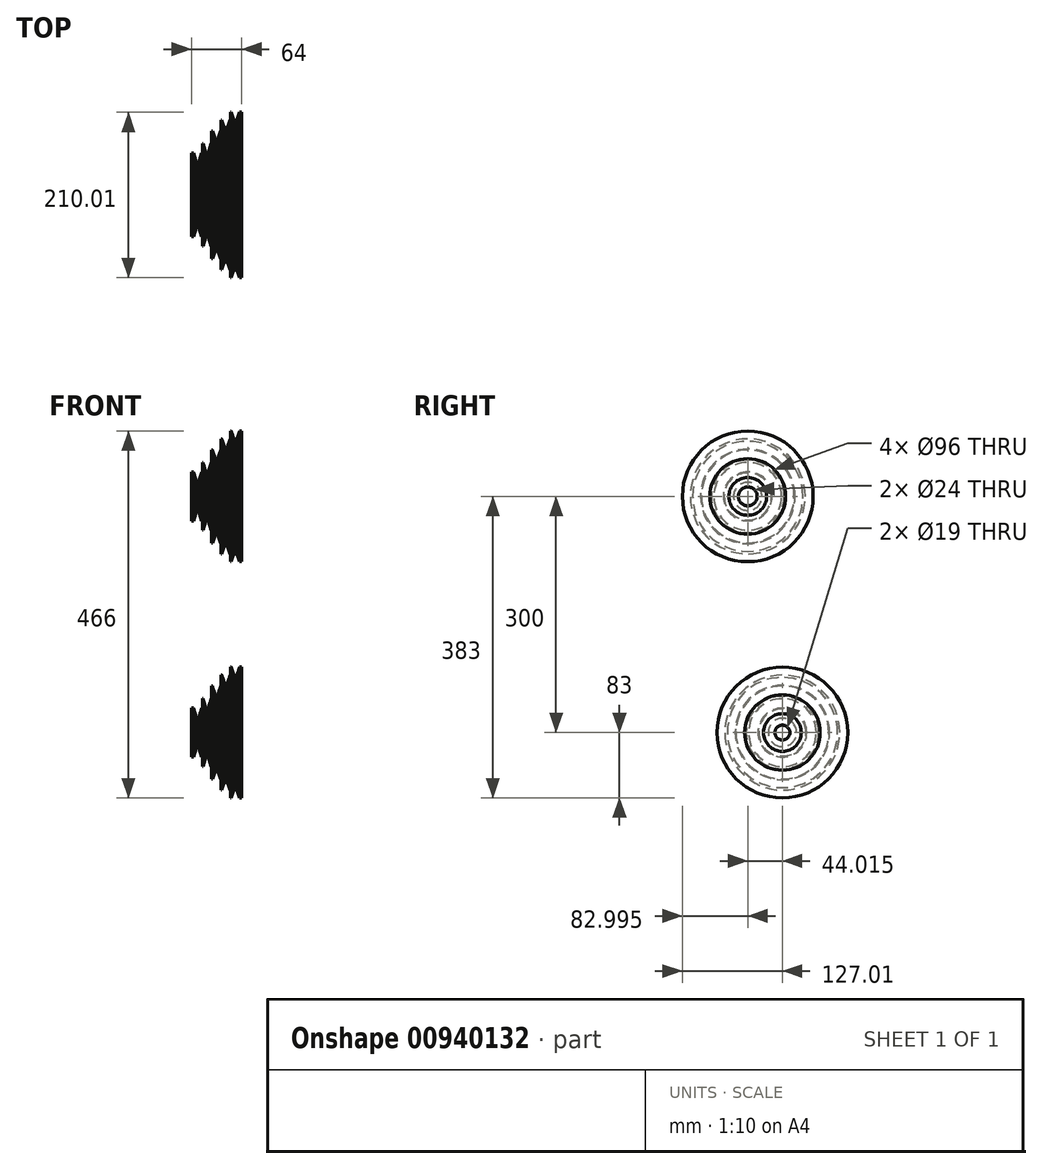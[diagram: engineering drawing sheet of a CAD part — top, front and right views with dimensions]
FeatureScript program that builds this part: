
annotation { "Feature Type Name" : "Feature", "Feature Type Description" : "" }
export const myFeature = defineFeature(function(context is Context, id is Id, definition is map)
    precondition{}
    {
        {
            var Q0;
            Q0=qCreatedBy(makeId("Top.planeOp"),FACE);
            var sketch = newSketch(context, id + "F0", { "sketchPlane" : qUnion([Q0])});
            skLineSegment(sketch, "E0", {"start": v(0, 0) * mm, "end": v(30, 0) * mm, "construction": true});
            skLineSegment(sketch, "E1", {"start": v(0, 0) * mm, "end": v(0, 31) * mm, "construction": true});
            skLineSegment(sketch, "E2", {"start": v(12, 0) * mm, "end": v(12, 31) * mm, "construction": true});
            skLineSegment(sketch, "E3", {"start": v(24, 0) * mm, "end": v(24, 43) * mm, "construction": true});
            skLineSegment(sketch, "E4", {"start": v(36, 0) * mm, "end": v(36, 59) * mm, "construction": true});
            skLineSegment(sketch, "E5", {"start": v(48, 0) * mm, "end": v(48, 73) * mm, "construction": true});
            skLineSegment(sketch, "E6", {"start": v(0, 31) * mm, "end": v(0.83, 31) * mm});
            skLineSegment(sketch, "E7", {"start": v(12, 43) * mm, "end": v(12.78, 43) * mm});
            skLineSegment(sketch, "E8", {"start": v(60, 0) * mm, "end": v(60, 83) * mm, "construction": true});
            skLineSegment(sketch, "E9", {"start": v(24, 59) * mm, "end": v(24.72, 59) * mm});
            skLineSegment(sketch, "E10", {"start": v(36, 73) * mm, "end": v(36.72, 73) * mm});
            skLineSegment(sketch, "E11", {"start": v(48, 83) * mm, "end": v(48.72, 83) * mm});
            skLineSegment(sketch, "E12", {"start": v(0, 28) * mm, "end": v(12, 28) * mm, "construction": true});
            skLineSegment(sketch, "E13", {"start": v(0, 18) * mm, "end": v(4.8, 18) * mm, "construction": true});
            skLineSegment(sketch, "E14", {"start": v(12, 40) * mm, "end": v(24, 40) * mm, "construction": true});
            skLineSegment(sketch, "E15", {"start": v(12, 30) * mm, "end": v(17, 30) * mm, "construction": true});
            skLineSegment(sketch, "E16", {"start": v(24, 56) * mm, "end": v(36, 56) * mm, "construction": true});
            skLineSegment(sketch, "E17", {"start": v(24, 46) * mm, "end": v(29.2, 46) * mm, "construction": true});
            skLineSegment(sketch, "E18", {"start": v(36, 70) * mm, "end": v(48, 70) * mm, "construction": true});
            skLineSegment(sketch, "E19", {"start": v(36, 60) * mm, "end": v(41.2, 60) * mm, "construction": true});
            skLineSegment(sketch, "E20", {"start": v(48, 80) * mm, "end": v(60, 80) * mm, "construction": true});
            skLineSegment(sketch, "E21", {"start": v(48, 70) * mm, "end": v(53.2, 70) * mm, "construction": true});
            skLineSegment(sketch, "E22", {"start": v(1.75, 28) * mm, "end": v(1.75, 28) * mm});
            skLineSegment(sketch, "E23", {"start": v(10.25, 28) * mm, "end": v(10.25, 28) * mm});
            skLineSegment(sketch, "E24", {"start": v(13.75, 40) * mm, "end": v(13.75, 30) * mm, "construction": true});
            skLineSegment(sketch, "E25", {"start": v(22.25, 40) * mm, "end": v(22.25, 30) * mm, "construction": true});
            skLineSegment(sketch, "E26", {"start": v(25.75, 56) * mm, "end": v(25.75, 46) * mm, "construction": true});
            skLineSegment(sketch, "E27", {"start": v(34.25, 56) * mm, "end": v(34.25, 46) * mm, "construction": true});
            skLineSegment(sketch, "E28", {"start": v(37.75, 70) * mm, "end": v(37.75, 60) * mm, "construction": true});
            skLineSegment(sketch, "E29", {"start": v(46.25, 70) * mm, "end": v(46.25, 60) * mm, "construction": true});
            skLineSegment(sketch, "E30", {"start": v(49.75, 80) * mm, "end": v(49.75, 70) * mm, "construction": true});
            skLineSegment(sketch, "E31", {"start": v(58.25, 80) * mm, "end": v(58.25, 70) * mm, "construction": true});
            skLineSegment(sketch, "E32", {"start": v(1.75, 28) * mm, "end": v(4.8, 18) * mm});
            skLineSegment(sketch, "E33", {"start": v(10.25, 28) * mm, "end": v(7.2, 18) * mm});
            skLineSegment(sketch, "E34", {"start": v(13.75, 40) * mm, "end": v(17, 30) * mm});
            skLineSegment(sketch, "E35", {"start": v(22.25, 40) * mm, "end": v(19, 30) * mm});
            skLineSegment(sketch, "E36", {"start": v(25.75, 56) * mm, "end": v(29.2, 46) * mm});
            skLineSegment(sketch, "E37", {"start": v(34.25, 56) * mm, "end": v(30.8, 46) * mm});
            skLineSegment(sketch, "E38", {"start": v(37.75, 70) * mm, "end": v(41.2, 60) * mm});
            skLineSegment(sketch, "E39", {"start": v(46.25, 70) * mm, "end": v(42.8, 60) * mm});
            skLineSegment(sketch, "E40", {"start": v(49.75, 80) * mm, "end": v(53.2, 70) * mm});
            skLineSegment(sketch, "E41", {"start": v(58.25, 80) * mm, "end": v(54.8, 70) * mm});
            skLineSegment(sketch, "E42", {"start": v(1.75, 28) * mm, "end": v(0.83, 31) * mm});
            skLineSegment(sketch, "E43", {"start": v(10.25, 28) * mm, "end": v(11.17, 31) * mm});
            skLineSegment(sketch, "E44", {"start": v(13.75, 40) * mm, "end": v(12.78, 43) * mm});
            skLineSegment(sketch, "E45", {"start": v(22.25, 40) * mm, "end": v(23.22, 43) * mm});
            skLineSegment(sketch, "E46", {"start": v(25.75, 56) * mm, "end": v(24.72, 59) * mm});
            skLineSegment(sketch, "E47", {"start": v(34.25, 56) * mm, "end": v(35.28, 59) * mm});
            skLineSegment(sketch, "E48", {"start": v(37.75, 70) * mm, "end": v(36.72, 73) * mm});
            skLineSegment(sketch, "E49", {"start": v(46.25, 70) * mm, "end": v(47.28, 73) * mm});
            skLineSegment(sketch, "E50", {"start": v(49.75, 80) * mm, "end": v(48.72, 83) * mm});
            skLineSegment(sketch, "E51", {"start": v(58.25, 80) * mm, "end": v(59.28, 83) * mm});
            skLineSegment(sketch, "E52", {"start": v(0.83, 31) * mm, "end": v(0.83, 31) * mm});
            skLineSegment(sketch, "E53", {"start": v(11.17, 31) * mm, "end": v(11.17, 31) * mm});
            skLineSegment(sketch, "E54", {"start": v(4.8, 18) * mm, "end": v(7.2, 18) * mm});
            skLineSegment(sketch, "E55", {"start": v(7.2, 18) * mm, "end": v(12, 18) * mm, "construction": true});
            skLineSegment(sketch, "E56", {"start": v(1.75, 28) * mm, "end": v(1.75, 18) * mm, "construction": true});
            skLineSegment(sketch, "E57", {"start": v(10.25, 28) * mm, "end": v(10.25, 18) * mm, "construction": true});
            skLineSegment(sketch, "E58", {"start": v(0.83, 31) * mm, "end": v(11.17, 31) * mm, "construction": true});
            skLineSegment(sketch, "E59", {"start": v(11.17, 31) * mm, "end": v(12, 31) * mm});
            skLineSegment(sketch, "E60", {"start": v(12.78, 43) * mm, "end": v(23.22, 43) * mm, "construction": true});
            skLineSegment(sketch, "E61", {"start": v(23.22, 43) * mm, "end": v(24, 43) * mm});
            skLineSegment(sketch, "E62", {"start": v(17, 30) * mm, "end": v(19, 30) * mm});
            skLineSegment(sketch, "E63", {"start": v(19, 30) * mm, "end": v(24, 30) * mm, "construction": true});
            skLineSegment(sketch, "E64", {"start": v(24.72, 59) * mm, "end": v(35.28, 59) * mm, "construction": true});
            skLineSegment(sketch, "E65", {"start": v(35.28, 59) * mm, "end": v(36, 59) * mm});
            skLineSegment(sketch, "E66", {"start": v(29.2, 46) * mm, "end": v(30.8, 46) * mm});
            skLineSegment(sketch, "E67", {"start": v(30.8, 46) * mm, "end": v(36, 46) * mm, "construction": true});
            skLineSegment(sketch, "E68", {"start": v(36.72, 73) * mm, "end": v(47.28, 73) * mm, "construction": true});
            skLineSegment(sketch, "E69", {"start": v(47.28, 73) * mm, "end": v(48, 73) * mm});
            skLineSegment(sketch, "E70", {"start": v(41.2, 60) * mm, "end": v(41.2, 60) * mm});
            skLineSegment(sketch, "E71", {"start": v(42.8, 60) * mm, "end": v(48, 60) * mm, "construction": true});
            skLineSegment(sketch, "E72", {"start": v(41.2, 60) * mm, "end": v(42.8, 60) * mm});
            skLineSegment(sketch, "E73", {"start": v(48.72, 83) * mm, "end": v(59.28, 83) * mm, "construction": true});
            skLineSegment(sketch, "E74", {"start": v(59.28, 83) * mm, "end": v(60, 83) * mm});
            skLineSegment(sketch, "E75", {"start": v(53.2, 70) * mm, "end": v(53.2, 70) * mm});
            skLineSegment(sketch, "E76", {"start": v(54.8, 70) * mm, "end": v(60, 70) * mm, "construction": true});
            skLineSegment(sketch, "E77", {"start": v(53.2, 70) * mm, "end": v(54.8, 70) * mm});
            skLineSegment(sketch, "E78", {"start": v(12, 31) * mm, "end": v(12, 31) * mm});
            skLineSegment(sketch, "E79", {"start": v(12, 31) * mm, "end": v(12, 43) * mm});
            skLineSegment(sketch, "E80", {"start": v(24, 43) * mm, "end": v(24, 59) * mm});
            skLineSegment(sketch, "E81", {"start": v(36, 59) * mm, "end": v(36, 73) * mm});
            skLineSegment(sketch, "E82", {"start": v(48, 73) * mm, "end": v(48, 83) * mm});
            skLineSegment(sketch, "E83", {"start": v(60, 0) * mm, "end": v(62, 0) * mm, "construction": true});
            skLineSegment(sketch, "E84", {"start": v(62, 0) * mm, "end": v(62, 48) * mm, "construction": true});
            skLineSegment(sketch, "E85", {"start": v(62, 83) * mm, "end": v(60, 83) * mm});
            skLineSegment(sketch, "E86", {"start": v(0, 0) * mm, "end": v(-2, 0) * mm, "construction": true});
            skLineSegment(sketch, "E87", {"start": v(-2, 0) * mm, "end": v(-2, 9.5) * mm, "construction": true});
            skLineSegment(sketch, "E88", {"start": v(-2, 31) * mm, "end": v(0, 31) * mm});
            skLineSegment(sketch, "E89", {"start": v(30, 0) * mm, "end": v(30, 9.5) * mm, "construction": true});
            skLineSegment(sketch, "E90", {"start": v(54, 0) * mm, "end": v(54, 48) * mm, "construction": true});
            skLineSegment(sketch, "E91", {"start": v(30, 24) * mm, "end": v(54, 48) * mm});
            skLineSegment(sketch, "E92", {"start": v(30, 0) * mm, "end": v(54, 0) * mm, "construction": true});
            skLineSegment(sketch, "E93", {"start": v(54, 0) * mm, "end": v(60, 0) * mm, "construction": true});
            skLineSegment(sketch, "E94", {"start": v(54, 48) * mm, "end": v(62, 48) * mm});
            skLineSegment(sketch, "E95", {"start": v(62, 48) * mm, "end": v(62, 83) * mm});
            skLineSegment(sketch, "E96", {"start": v(-2, 9.5) * mm, "end": v(-2, 9.5) * mm});
            skLineSegment(sketch, "E97", {"start": v(-2, 9.5) * mm, "end": v(30, 9.5) * mm});
            skLineSegment(sketch, "E98", {"start": v(-2, 9.5) * mm, "end": v(-2, 31) * mm});
            skLineSegment(sketch, "E99", {"start": v(30, 9.5) * mm, "end": v(30, 9.5) * mm});
            skLineSegment(sketch, "E100", {"start": v(30, 9.5) * mm, "end": v(30, 24) * mm});
            skSolve(sketch);
        }
        {
            var Q0;
            Q0=makeQuery(id+"F0.imprint","IMPRINT",FACE,{"disambiguationData":[TD([[makeQuery(id+"F0.imprint","IMPRINT",EDGE,{"derivedFrom":sQuery(id+"F0.wireOp",EDGE,"E6")}),-1.0]])]});
            var Q1;
            Q1=sQuery(id+"F0.wireOp",EDGE,"E0");
            revolve(context, id + "F1", {"surfaceOperationType" : NewSurfaceOperationType.NEW, "entities" : qUnion([Q0]), "axis" : qUnion([Q1]), "revolveType" : RevolveType.FULL});
        }
        {
            var Q0;
            Q0=qCreatedBy(makeId("Top.planeOp"),FACE);
            cPlane(context, id + "F2", {"entities" : qUnion([Q0]), "cplaneType" : CPlaneType.OFFSET, "offset" : 300 * mm, "width" : 150 * mm, "height" : 150 * mm});
        }
        {
            var Q0;
            Q0=qCreatedBy(id+"F2.planeOp",FACE);
            var sketch = newSketch(context, id + "F3", { "sketchPlane" : qUnion([Q0])});
            skLineSegment(sketch, "E101", {"start": v(0, -44.01) * mm, "end": v(30, -44.01) * mm, "construction": true});
            skLineSegment(sketch, "E102", {"start": v(0, -44.01) * mm, "end": v(0, -13.01) * mm, "construction": true});
            skLineSegment(sketch, "E103", {"start": v(12, -44.01) * mm, "end": v(12, -13.01) * mm, "construction": true});
            skLineSegment(sketch, "E104", {"start": v(24, -44.01) * mm, "end": v(24, -1.01) * mm, "construction": true});
            skLineSegment(sketch, "E105", {"start": v(36, -44.01) * mm, "end": v(36, 14.99) * mm, "construction": true});
            skLineSegment(sketch, "E106", {"start": v(48, -44.01) * mm, "end": v(48, 28.99) * mm, "construction": true});
            skLineSegment(sketch, "E107", {"start": v(0, -13.01) * mm, "end": v(0.83, -13.01) * mm});
            skLineSegment(sketch, "E108", {"start": v(12, -1.01) * mm, "end": v(12.78, -1.01) * mm});
            skLineSegment(sketch, "E109", {"start": v(60, -44.01) * mm, "end": v(60, 38.99) * mm, "construction": true});
            skLineSegment(sketch, "E110", {"start": v(24, 14.99) * mm, "end": v(24.72, 14.99) * mm});
            skLineSegment(sketch, "E111", {"start": v(36, 28.99) * mm, "end": v(36.72, 28.99) * mm});
            skLineSegment(sketch, "E112", {"start": v(48, 38.99) * mm, "end": v(48.72, 38.99) * mm});
            skLineSegment(sketch, "E113", {"start": v(0, -16.01) * mm, "end": v(12, -16.01) * mm, "construction": true});
            skLineSegment(sketch, "E114", {"start": v(0, -26.01) * mm, "end": v(4.8, -26.01) * mm, "construction": true});
            skLineSegment(sketch, "E115", {"start": v(12, -4.01) * mm, "end": v(24, -4.01) * mm, "construction": true});
            skLineSegment(sketch, "E116", {"start": v(12, -14.01) * mm, "end": v(17, -14.01) * mm, "construction": true});
            skLineSegment(sketch, "E117", {"start": v(24, 11.99) * mm, "end": v(36, 11.99) * mm, "construction": true});
            skLineSegment(sketch, "E118", {"start": v(24, 1.99) * mm, "end": v(29.2, 1.99) * mm, "construction": true});
            skLineSegment(sketch, "E119", {"start": v(36, 25.99) * mm, "end": v(48, 25.99) * mm, "construction": true});
            skLineSegment(sketch, "E120", {"start": v(36, 15.99) * mm, "end": v(41.2, 15.99) * mm, "construction": true});
            skLineSegment(sketch, "E121", {"start": v(48, 35.99) * mm, "end": v(60, 35.99) * mm, "construction": true});
            skLineSegment(sketch, "E122", {"start": v(48, 25.99) * mm, "end": v(53.2, 25.99) * mm, "construction": true});
            skLineSegment(sketch, "E123", {"start": v(1.75, -16.01) * mm, "end": v(1.75, -16.01) * mm});
            skLineSegment(sketch, "E124", {"start": v(10.25, -16.01) * mm, "end": v(10.25, -16.01) * mm});
            skLineSegment(sketch, "E125", {"start": v(13.75, -4.01) * mm, "end": v(13.75, -14.01) * mm, "construction": true});
            skLineSegment(sketch, "E126", {"start": v(22.25, -4.01) * mm, "end": v(22.25, -14.01) * mm, "construction": true});
            skLineSegment(sketch, "E127", {"start": v(25.75, 11.99) * mm, "end": v(25.75, 1.99) * mm, "construction": true});
            skLineSegment(sketch, "E128", {"start": v(34.25, 11.99) * mm, "end": v(34.25, 1.99) * mm, "construction": true});
            skLineSegment(sketch, "E129", {"start": v(37.75, 25.99) * mm, "end": v(37.75, 15.99) * mm, "construction": true});
            skLineSegment(sketch, "E130", {"start": v(46.25, 25.99) * mm, "end": v(46.25, 15.99) * mm, "construction": true});
            skLineSegment(sketch, "E131", {"start": v(49.75, 35.99) * mm, "end": v(49.75, 25.99) * mm, "construction": true});
            skLineSegment(sketch, "E132", {"start": v(58.25, 35.99) * mm, "end": v(58.25, 25.99) * mm, "construction": true});
            skLineSegment(sketch, "E133", {"start": v(1.75, -16.01) * mm, "end": v(4.8, -26.01) * mm});
            skLineSegment(sketch, "E134", {"start": v(10.25, -16.01) * mm, "end": v(7.2, -26.01) * mm});
            skLineSegment(sketch, "E135", {"start": v(13.75, -4.01) * mm, "end": v(17, -14.01) * mm});
            skLineSegment(sketch, "E136", {"start": v(22.25, -4.01) * mm, "end": v(19, -14.01) * mm});
            skLineSegment(sketch, "E137", {"start": v(25.75, 11.99) * mm, "end": v(29.2, 1.99) * mm});
            skLineSegment(sketch, "E138", {"start": v(34.25, 11.99) * mm, "end": v(30.8, 1.99) * mm});
            skLineSegment(sketch, "E139", {"start": v(37.75, 25.99) * mm, "end": v(41.2, 15.99) * mm});
            skLineSegment(sketch, "E140", {"start": v(46.25, 25.99) * mm, "end": v(42.8, 15.99) * mm});
            skLineSegment(sketch, "E141", {"start": v(49.75, 35.99) * mm, "end": v(53.2, 25.99) * mm});
            skLineSegment(sketch, "E142", {"start": v(58.25, 35.99) * mm, "end": v(54.8, 25.99) * mm});
            skLineSegment(sketch, "E143", {"start": v(1.75, -16.01) * mm, "end": v(0.83, -13.01) * mm});
            skLineSegment(sketch, "E144", {"start": v(10.25, -16.01) * mm, "end": v(11.17, -13.01) * mm});
            skLineSegment(sketch, "E145", {"start": v(13.75, -4.01) * mm, "end": v(12.78, -1.01) * mm});
            skLineSegment(sketch, "E146", {"start": v(22.25, -4.01) * mm, "end": v(23.22, -1.01) * mm});
            skLineSegment(sketch, "E147", {"start": v(25.75, 11.99) * mm, "end": v(24.72, 14.99) * mm});
            skLineSegment(sketch, "E148", {"start": v(34.25, 11.99) * mm, "end": v(35.28, 14.99) * mm});
            skLineSegment(sketch, "E149", {"start": v(37.75, 25.99) * mm, "end": v(36.72, 28.99) * mm});
            skLineSegment(sketch, "E150", {"start": v(46.25, 25.99) * mm, "end": v(47.28, 28.99) * mm});
            skLineSegment(sketch, "E151", {"start": v(49.75, 35.99) * mm, "end": v(48.72, 38.99) * mm});
            skLineSegment(sketch, "E152", {"start": v(58.25, 35.99) * mm, "end": v(59.28, 38.99) * mm});
            skLineSegment(sketch, "E153", {"start": v(0.83, -13.01) * mm, "end": v(0.83, -13.01) * mm});
            skLineSegment(sketch, "E154", {"start": v(11.17, -13.01) * mm, "end": v(11.17, -13.01) * mm});
            skLineSegment(sketch, "E155", {"start": v(4.8, -26.01) * mm, "end": v(7.2, -26.01) * mm});
            skLineSegment(sketch, "E156", {"start": v(7.2, -26.01) * mm, "end": v(12, -26.01) * mm, "construction": true});
            skLineSegment(sketch, "E157", {"start": v(1.75, -16.01) * mm, "end": v(1.75, -26.01) * mm, "construction": true});
            skLineSegment(sketch, "E158", {"start": v(10.25, -16.01) * mm, "end": v(10.25, -26.01) * mm, "construction": true});
            skLineSegment(sketch, "E159", {"start": v(0.83, -13.01) * mm, "end": v(11.17, -13.01) * mm, "construction": true});
            skLineSegment(sketch, "E160", {"start": v(11.17, -13.01) * mm, "end": v(12, -13.01) * mm});
            skLineSegment(sketch, "E161", {"start": v(12.78, -1.01) * mm, "end": v(23.22, -1.01) * mm, "construction": true});
            skLineSegment(sketch, "E162", {"start": v(23.22, -1.01) * mm, "end": v(24, -1.01) * mm});
            skLineSegment(sketch, "E163", {"start": v(17, -14.01) * mm, "end": v(19, -14.01) * mm});
            skLineSegment(sketch, "E164", {"start": v(19, -14.01) * mm, "end": v(24, -14.01) * mm, "construction": true});
            skLineSegment(sketch, "E165", {"start": v(24.72, 14.99) * mm, "end": v(35.28, 14.99) * mm, "construction": true});
            skLineSegment(sketch, "E166", {"start": v(35.28, 14.99) * mm, "end": v(36, 14.99) * mm});
            skLineSegment(sketch, "E167", {"start": v(29.2, 1.99) * mm, "end": v(30.8, 1.99) * mm});
            skLineSegment(sketch, "E168", {"start": v(30.8, 1.99) * mm, "end": v(36, 1.99) * mm, "construction": true});
            skLineSegment(sketch, "E169", {"start": v(36.72, 28.99) * mm, "end": v(47.28, 28.99) * mm, "construction": true});
            skLineSegment(sketch, "E170", {"start": v(47.28, 28.99) * mm, "end": v(48, 28.99) * mm});
            skLineSegment(sketch, "E171", {"start": v(41.2, 15.99) * mm, "end": v(41.2, 15.99) * mm});
            skLineSegment(sketch, "E172", {"start": v(42.8, 15.99) * mm, "end": v(48, 15.99) * mm, "construction": true});
            skLineSegment(sketch, "E173", {"start": v(41.2, 15.99) * mm, "end": v(42.8, 15.99) * mm});
            skLineSegment(sketch, "E174", {"start": v(48.72, 38.99) * mm, "end": v(59.28, 38.99) * mm, "construction": true});
            skLineSegment(sketch, "E175", {"start": v(59.28, 38.99) * mm, "end": v(60, 38.99) * mm});
            skLineSegment(sketch, "E176", {"start": v(53.2, 25.99) * mm, "end": v(53.2, 25.99) * mm});
            skLineSegment(sketch, "E177", {"start": v(54.8, 25.99) * mm, "end": v(60, 25.99) * mm, "construction": true});
            skLineSegment(sketch, "E178", {"start": v(53.2, 25.99) * mm, "end": v(54.8, 25.99) * mm});
            skLineSegment(sketch, "E179", {"start": v(12, -13.01) * mm, "end": v(12, -13.01) * mm});
            skLineSegment(sketch, "E180", {"start": v(12, -13.01) * mm, "end": v(12, -1.01) * mm});
            skLineSegment(sketch, "E181", {"start": v(24, -1.01) * mm, "end": v(24, 14.99) * mm});
            skLineSegment(sketch, "E182", {"start": v(36, 14.99) * mm, "end": v(36, 28.99) * mm});
            skLineSegment(sketch, "E183", {"start": v(48, 28.99) * mm, "end": v(48, 38.99) * mm});
            skLineSegment(sketch, "E184", {"start": v(60, -44.01) * mm, "end": v(62, -44.01) * mm, "construction": true});
            skLineSegment(sketch, "E185", {"start": v(62, -44.01) * mm, "end": v(62, 3.99) * mm, "construction": true});
            skLineSegment(sketch, "E186", {"start": v(62, 38.99) * mm, "end": v(60, 38.99) * mm});
            skLineSegment(sketch, "E187", {"start": v(0, -44.01) * mm, "end": v(-2, -44.01) * mm, "construction": true});
            skLineSegment(sketch, "E188", {"start": v(-2, -44.01) * mm, "end": v(-2, -32.01) * mm, "construction": true});
            skLineSegment(sketch, "E189", {"start": v(-2, -13.01) * mm, "end": v(0, -13.01) * mm});
            skLineSegment(sketch, "E190", {"start": v(30, -44.01) * mm, "end": v(30, -32.01) * mm, "construction": true});
            skLineSegment(sketch, "E191", {"start": v(54, -44.01) * mm, "end": v(54, 3.99) * mm, "construction": true});
            skLineSegment(sketch, "E192", {"start": v(30, -20.01) * mm, "end": v(54, 3.99) * mm});
            skLineSegment(sketch, "E193", {"start": v(30, -44.01) * mm, "end": v(54, -44.01) * mm, "construction": true});
            skLineSegment(sketch, "E194", {"start": v(54, -44.01) * mm, "end": v(60, -44.01) * mm, "construction": true});
            skLineSegment(sketch, "E195", {"start": v(54, 3.99) * mm, "end": v(62, 3.99) * mm});
            skLineSegment(sketch, "E196", {"start": v(62, 3.99) * mm, "end": v(62, 38.99) * mm});
            skLineSegment(sketch, "E197", {"start": v(-2, -32.01) * mm, "end": v(-2, -32.01) * mm});
            skLineSegment(sketch, "E198", {"start": v(-2, -32.01) * mm, "end": v(30, -32.01) * mm});
            skLineSegment(sketch, "E199", {"start": v(-2, -32.01) * mm, "end": v(-2, -13.01) * mm});
            skLineSegment(sketch, "E200", {"start": v(30, -32.01) * mm, "end": v(30, -32.01) * mm});
            skLineSegment(sketch, "E201", {"start": v(30, -32.01) * mm, "end": v(30, -20.01) * mm});
            skSolve(sketch);
        }
        {
            var Q0;
            Q0=makeQuery(id+"F3.imprint","IMPRINT",FACE,{"disambiguationData":[TD([[makeQuery(id+"F3.imprint","IMPRINT",EDGE,{"derivedFrom":sQuery(id+"F3.wireOp",EDGE,"E107")}),-1.0]])]});
            var Q1;
            Q1=sQuery(id+"F3.wireOp",EDGE,"E101");
            revolve(context, id + "F4", {"surfaceOperationType" : NewSurfaceOperationType.NEW, "entities" : qUnion([Q0]), "axis" : qUnion([Q1]), "revolveType" : RevolveType.FULL});
        }
    });
